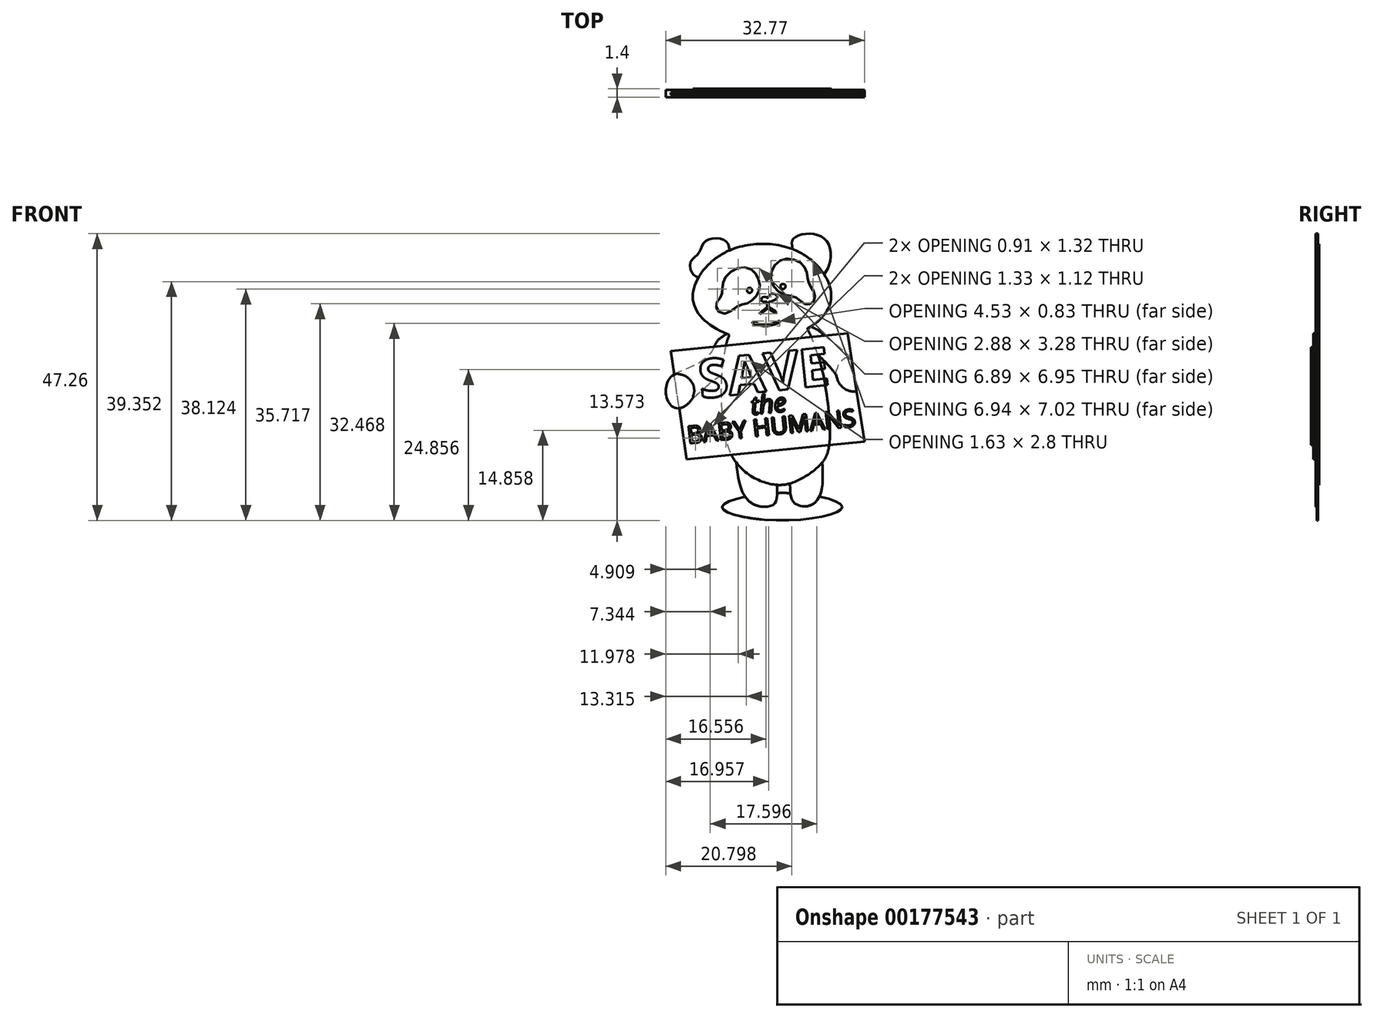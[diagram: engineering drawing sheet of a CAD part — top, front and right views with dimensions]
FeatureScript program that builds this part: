
annotation { "Feature Type Name" : "Feature", "Feature Type Description" : "" }
export const myFeature = defineFeature(function(context is Context, id is Id, definition is map)
    precondition{}
    {
        {
            var Q0;
            Q0=qCreatedBy(makeId("Front.planeOp"),FACE);
            var sketch = newSketch(context, id + "F0", { "sketchPlane" : qUnion([Q0])});
            skFitSpline(sketch, "E0", {"points": [v(-5.28, 20.68) * mm, v(-7.35, 19.05) * mm, v(-7.73, 17.53) * mm, v(-7.93, 16.12) * mm, v(-8.6, 15.23) * mm, v(-8.65, 13.83) * mm, v(-7.17, 13.2) * mm, v(-5.14, 14.5) * mm, v(-3.7, 14.88) * mm, v(-2.4, 15.83) * mm, v(-1.67, 17.32) * mm, v(-1.8, 18.83) * mm, v(-2.96, 20.4) * mm, v(-5.28, 20.68) * mm]});
            skCircle(sketch, "E1", {"center": v(-3.3, 17.01) * mm, "radius": 0.42 * mm});
            skPoint(sketch, "E1.first.point", {"position": v(-3.3, 17.43) * mm});
            skPoint(sketch, "E1.second.point", {"position": v(-3.71, 16.96) * mm});
            skPoint(sketch, "E1.third.point", {"position": v(-2.98, 16.74) * mm});
            skFitSpline(sketch, "E2", {"points": [v(1.76, 21.94) * mm, v(0.2, 19.14) * mm, v(2.09, 16.4) * mm, v(4.27, 15.86) * mm, v(5.92, 14.74) * mm, v(7.23, 15.16) * mm, v(7.35, 16.75) * mm, v(6.47, 18.12) * mm, v(6.17, 19.96) * mm, v(4.8, 21.76) * mm, v(1.76, 21.94) * mm]});
            skCircle(sketch, "E3", {"center": v(2.22, 17.66) * mm, "radius": 0.42 * mm});
            skPoint(sketch, "E3.first.point", {"position": v(2.1, 18.06) * mm});
            skPoint(sketch, "E3.second.point", {"position": v(2.6, 17.5) * mm});
            skPoint(sketch, "E3.third.point", {"position": v(1.93, 17.36) * mm});
            skArc(sketch, "E4", {"start": v(-2.65, 11.8) * mm, "mid": v(-0.55, 11.38) * mm, "end": v(1.52, 11.95) * mm});
            skArc(sketch, "E5.0", {"start": v(-2.76, 11.58) * mm, "mid": v(-0.54, 11.13) * mm, "end": v(1.64, 11.73) * mm});
            skArc(sketch, "E6", {"start": v(-2.65, 11.8) * mm, "mid": v(-2.82, 11.75) * mm, "end": v(-2.76, 11.58) * mm});
            skArc(sketch, "E7", {"start": v(1.64, 11.73) * mm, "mid": v(1.69, 11.9) * mm, "end": v(1.52, 11.95) * mm});
            skLineSegment(sketch, "E8", {"start": v(-0.37, 15.1) * mm, "end": v(-0.37, 14.25) * mm});
            skLineSegment(sketch, "E9", {"start": v(-0.37, 14.25) * mm, "end": v(-1.56, 13.38) * mm});
            skLineSegment(sketch, "E10", {"start": v(-1.4, 13.18) * mm, "end": v(-0.25, 14.04) * mm});
            skLineSegment(sketch, "E11", {"start": v(-0.25, 14.04) * mm, "end": v(0.84, 13.34) * mm});
            skLineSegment(sketch, "E12", {"start": v(0.97, 13.55) * mm, "end": v(-0.12, 14.25) * mm});
            skArc(sketch, "E13", {"start": v(-1.56, 13.38) * mm, "mid": v(-1.58, 13.2) * mm, "end": v(-1.4, 13.18) * mm});
            skArc(sketch, "E14", {"start": v(0.84, 13.34) * mm, "mid": v(1.01, 13.38) * mm, "end": v(0.97, 13.55) * mm});
            skLineSegment(sketch, "E15", {"start": v(-0.12, 14.25) * mm, "end": v(-0.12, 15.1) * mm});
            skLineSegment(sketch, "E16", {"start": v(-0.12, 14.25) * mm, "end": v(-0.37, 14.25) * mm, "construction": true});
            skLineSegment(sketch, "E17", {"start": v(-0.25, 14.04) * mm, "end": v(-0.25, 14.25) * mm, "construction": true});
            skFitSpline(sketch, "E18", {"points": [v(-0.12, 15.1) * mm, v(0.96, 15.47) * mm, v(1.28, 16) * mm, v(0.76, 16.41) * mm, v(0.1, 16.32) * mm, v(-0.34, 15.75) * mm, v(-0.55, 15.87) * mm, v(-1.21, 15.83) * mm, v(-1.3, 15.26) * mm, v(-0.37, 15.1) * mm], "startDerivative": vector(11.63, 3.5) * mm, "endDerivative": vector(9.76, -0.12) * mm});
            skFitSpline(sketch, "E19", {"points": [v(-2.63, 24.6) * mm, v(-9.81, 21.5) * mm, v(-12.55, 14.98) * mm, v(-4.94, 9.22) * mm, v(7.09, 11.26) * mm, v(10.15, 16.53) * mm, v(5.87, 22.76) * mm, v(-2.63, 24.6) * mm]});
            skFitSpline(sketch, "E20", {"points": [v(9.02, 19.63) * mm, v(10.01, 21.92) * mm, v(9.55, 24.92) * mm, v(7.54, 26.24) * mm, v(4.8, 26.07) * mm, v(3.75, 25.22) * mm, v(3.79, 23.8) * mm], "startDerivative": vector(7.2, 11.9) * mm, "endDerivative": vector(1.85, -11.75) * mm});
            skFitSpline(sketch, "E21", {"points": [v(-6.58, 23.6) * mm, v(-7.17, 25.08) * mm, v(-9.3, 25.6) * mm, v(-10.91, 24.76) * mm, v(-11.7, 23.08) * mm, v(-12.97, 21.79) * mm, v(-12.73, 19.83) * mm, v(-11.73, 19.13) * mm], "startDerivative": vector(-2.26, 12.84) * mm, "endDerivative": vector(9.74, -4.03) * mm});
            skLineSegment(sketch, "E22", {"start": v(-16.26, 7) * mm, "end": v(12.87, 9.94) * mm});
            skLineSegment(sketch, "E23", {"start": v(12.87, 9.94) * mm, "end": v(15.65, -7.93) * mm});
            skLineSegment(sketch, "E24", {"start": v(15.65, -7.93) * mm, "end": v(-13.67, -10.86) * mm});
            skLineSegment(sketch, "E25", {"start": v(-13.67, -10.86) * mm, "end": v(-16.26, 7) * mm});
            skFitSpline(sketch, "E26", {"points": [v(-6.63, 9.7) * mm, v(-7.92, -2.36) * mm, v(-5.2, -11.77) * mm, v(1.02, -15.04) * mm, v(4.98, -14.16) * mm, v(8.4, -11.7) * mm, v(9.84, -8.51) * mm, v(9.3, 0.7) * mm, v(6.24, 10.75) * mm], "startDerivative": vector(-22.93, -59.57) * mm, "endDerivative": vector(-34.57, 71.29) * mm});
            skFitSpline(sketch, "E27", {"points": [v(1.24, -15.06) * mm, v(1.05, -17.83) * mm, v(0.16, -18.54) * mm, v(-1.53, -18.61) * mm, v(-3.1, -17.97) * mm, v(-4.6, -15.86) * mm, v(-5.5, -11.37) * mm], "startDerivative": vector(0.14, -22.55) * mm, "endDerivative": vector(-2, 15.97) * mm});
            skFitSpline(sketch, "E28", {"points": [v(3.35, -14.83) * mm, v(3.85, -17.76) * mm, v(5.22, -18.57) * mm, v(7.4, -18.06) * mm, v(8.67, -15.36) * mm, v(8.68, -11.38) * mm], "startDerivative": vector(0.57, -23.36) * mm, "endDerivative": vector(-0.75, 13.96) * mm});
            skFitSpline(sketch, "E29", {"points": [v(-7.08, 9.86) * mm, v(-8.5, 8.78) * mm, v(-9.06, 7.87) * mm, v(-9.71, 6.7) * mm, v(-11.13, 5.35) * mm, v(-13.33, 4.22) * mm, v(-15.15, 3.31) * mm, v(-13.96, 2.94) * mm, v(-12.6, 1.46) * mm, v(-12.43, 0.2) * mm, v(-12.59, -0.63) * mm, v(-7.9, 3.1) * mm], "startDerivative": vector(-20.24, -14.92) * mm, "endDerivative": vector(48, 30.85) * mm});
            skFitSpline(sketch, "E30", {"points": [v(6.73, 11.03) * mm, v(8.93, 9.71) * mm, v(13.27, 6.03) * mm, v(12.9, 6) * mm, v(11.36, 4.7) * mm, v(11, 3.2) * mm, v(8.01, 6.33) * mm], "startDerivative": vector(19.92, -7.63) * mm, "endDerivative": vector(-37.46, 34.17) * mm});
            skFitSpline(sketch, "E31", {"points": [v(-15.15, 3.31) * mm, v(-16.84, 1.82) * mm, v(-17, -0.51) * mm, v(-15.8, -2.28) * mm, v(-14.43, -2.3) * mm, v(-12.59, -0.63) * mm], "startDerivative": vector(-13.86, -3.67) * mm, "endDerivative": vector(8.5, 13.26) * mm});
            skFitSpline(sketch, "E32", {"points": [v(13.27, 6.03) * mm, v(15.18, 4.93) * mm, v(15.77, 2.37) * mm, v(14.8, 0.57) * mm, v(13.17, 0.44) * mm, v(10.97, 3.13) * mm], "startDerivative": vector(17.85, -0.45) * mm, "endDerivative": vector(-4.75, 22.55) * mm});
            skFitSpline(sketch, "E33.trimOffspring", {"points": [v(-7.08, 9.86) * mm, v(-8.5, 8.78) * mm, v(-9.06, 7.87) * mm, v(-9.71, 6.7) * mm, v(-11.13, 5.35) * mm, v(-13.33, 4.22) * mm, v(-15.15, 3.31) * mm, v(-13.96, 2.94) * mm, v(-12.6, 1.46) * mm, v(-12.43, 0.2) * mm, v(-12.59, -0.63) * mm, v(-7.9, 3.1) * mm], "startDerivative": vector(-20.24, -14.92) * mm, "endDerivative": vector(48, 30.85) * mm});
            skFitSpline(sketch, "E34", {"points": [v(-15.15, 3.31) * mm, v(-13.96, 2.94) * mm, v(-12.87, 1.95) * mm, v(-12.43, 0.77) * mm, v(-12.59, -0.63) * mm], "startDerivative": vector(4.13, 0.65) * mm, "endDerivative": vector(-1.58, -1.83) * mm});
            skFitSpline(sketch, "E35", {"points": [v(10.97, 3.13) * mm, v(11.69, 4.98) * mm, v(13.27, 6.03) * mm], "startDerivative": vector(-0.55, 3.17) * mm, "endDerivative": vector(2.92, 0.17) * mm});
            skSolve(sketch);
        }
        {
            var Q0;
            Q0=makeQuery(id+"F0.imprint","IMPRINT",FACE,{"disambiguationData":[TD([[makeQuery(id+"F0.imprint","IMPRINT",EDGE,{"derivedFrom":sQuery(id+"F0.wireOp",EDGE,"E0")}),-1.0]])]});
            var Q1;
            Q1=makeQuery(id+"F0.imprint","IMPRINT",FACE,{"disambiguationData":[TD([[makeQuery(id+"F0.imprint","IMPRINT",EDGE,{"derivedFrom":sQuery(id+"F0.wireOp",EDGE,"E1")}),1.0]])]});
            var Q2;
            Q2=makeQuery(id+"F0.imprint","IMPRINT",FACE,{"disambiguationData":[TD([[makeQuery(id+"F0.imprint","IMPRINT",EDGE,{"derivedFrom":sQuery(id+"F0.wireOp",EDGE,"E3")}),1.0]])]});
            var Q3;
            {var subQ1=sQuery(id+"F0.wireOp",EDGE,"E26");var subQ7=sQuery(id+"F0.wireOp",EDGE,"E24");var subQ9=makeQuery(id+"F0.imprint","INTERSECT",VERTEX,{"disambiguationData":[OD(0.0)],"derivedFrom":[subQ7,subQ1]});Q3=makeQuery(id+"F0.imprint","IMPRINT",FACE,{"disambiguationData":[TD([[makeQuery(id+"F0.imprint","IMPRINT",EDGE,{"disambiguationData":[TD([[subQ9,-1.0]])],"derivedFrom":subQ7}),1.0]])]});}
            var Q4;
            {var subQ0=sQuery(id+"F0.wireOp",EDGE,"E26");var subQ1=sQuery(id+"F0.wireOp",EDGE,"E22");var subQ2=makeQuery(id+"F0.imprint","INTERSECT",VERTEX,{"disambiguationData":[OD(0.0)],"derivedFrom":[subQ1,subQ0]});Q4=makeQuery(id+"F0.imprint","IMPRINT",FACE,{"disambiguationData":[TD([[makeQuery(id+"F0.imprint","IMPRINT",EDGE,{"disambiguationData":[TD([[subQ2,-1.0]])],"derivedFrom":subQ1}),-1.0]])]});}
            var Q5;
            {var subQ0=sQuery(id+"F0.wireOp",EDGE,"E26");var subQ1=sQuery(id+"F0.wireOp",EDGE,"E19");var subQ2=makeQuery(id+"F0.imprint","INTERSECT",VERTEX,{"disambiguationData":[OD(0.0)],"derivedFrom":[subQ1,subQ0]});Q5=makeQuery(id+"F0.imprint","IMPRINT",FACE,{"disambiguationData":[TD([[makeQuery(id+"F0.imprint","IMPRINT",EDGE,{"disambiguationData":[TD([[subQ2,-1.0]])],"derivedFrom":subQ1}),-1.0]])]});}
            extrude(context, id + "F1", {"entities" : qUnion([Q0, Q1, Q2, Q3, Q4, Q5]), "depth" : .4 * mm});
        }
        {
            var Q0;
            Q0=makeQuery(id+"F0.imprint","IMPRINT",FACE,{"disambiguationData":[TD([[makeQuery(id+"F0.imprint","IMPRINT",EDGE,{"derivedFrom":sQuery(id+"F0.wireOp",EDGE,"E0")}),1.0]])]});
            var Q1;
            Q1=makeQuery(id+"F0.imprint","IMPRINT",FACE,{"disambiguationData":[TD([[makeQuery(id+"F0.imprint","IMPRINT",EDGE,{"derivedFrom":sQuery(id+"F0.wireOp",EDGE,"E2")}),1.0]])]});
            var Q2;
            {var subQ0=sQuery(id+"F0.wireOp",EDGE,"E20");Q2=makeQuery(id+"F0.imprint","IMPRINT",FACE,{"disambiguationData":[TD([[makeQuery(id+"F0.imprint","IMPRINT",EDGE,{"derivedFrom":subQ0}),1.0]])]});}
            var Q3;
            {var subQ0=sQuery(id+"F0.wireOp",EDGE,"E21");Q3=makeQuery(id+"F0.imprint","IMPRINT",FACE,{"disambiguationData":[TD([[makeQuery(id+"F0.imprint","IMPRINT",EDGE,{"derivedFrom":subQ0}),1.0]])]});}
            var Q4;
            Q4=makeQuery(id+"F0.imprint","IMPRINT",FACE,{"disambiguationData":[TD([[makeQuery(id+"F0.imprint","IMPRINT",EDGE,{"derivedFrom":sQuery(id+"F0.wireOp",EDGE,"E8")}),1.0]])]});
            var Q5;
            Q5=makeQuery(id+"F0.imprint","IMPRINT",FACE,{"disambiguationData":[TD([[makeQuery(id+"F0.imprint","IMPRINT",EDGE,{"derivedFrom":sQuery(id+"F0.wireOp",EDGE,"E4")}),-1.0]])]});
            var Q6;
            {var subQ0=sQuery(id+"F0.wireOp",EDGE,"E27");Q6=makeQuery(id+"F0.imprint","IMPRINT",FACE,{"disambiguationData":[TD([[makeQuery(id+"F0.imprint","IMPRINT",EDGE,{"derivedFrom":subQ0}),-1.0]])]});}
            var Q7;
            {var subQ0=sQuery(id+"F0.wireOp",EDGE,"E28");Q7=makeQuery(id+"F0.imprint","IMPRINT",FACE,{"disambiguationData":[TD([[makeQuery(id+"F0.imprint","IMPRINT",EDGE,{"derivedFrom":subQ0}),1.0]])]});}
            extrude(context, id + "F2", {"entities" : qUnion([Q0, Q1, Q2, Q3, Q4, Q5, Q6, Q7]), "depth" : .4 * mm});
        }
        {
            var Q0;
            {var subQ0=sQuery(id+"F0.wireOp",EDGE,"E29");var subQ1=sQuery(id+"F0.wireOp",EDGE,"E22");var subQ2=makeQuery(id+"F0.imprint","INTERSECT",VERTEX,{"derivedFrom":[subQ1,subQ0]});Q0=makeQuery(id+"F0.imprint","IMPRINT",FACE,{"disambiguationData":[TD([[makeQuery(id+"F0.imprint","IMPRINT",EDGE,{"disambiguationData":[TD([[subQ2,-1.0]])],"derivedFrom":subQ1}),-1.0]])]});}
            var Q1;
            {var subQ0=sQuery(id+"F0.wireOp",EDGE,"E26");var subQ1=sQuery(id+"F0.wireOp",EDGE,"E19");var subQ2=makeQuery(id+"F0.imprint","INTERSECT",VERTEX,{"disambiguationData":[OD(0.0)],"derivedFrom":[subQ1,subQ0]});Q1=makeQuery(id+"F0.imprint","IMPRINT",FACE,{"disambiguationData":[TD([[makeQuery(id+"F0.imprint","IMPRINT",EDGE,{"disambiguationData":[TD([[subQ2,1.0]])],"derivedFrom":subQ1}),-1.0]])]});}
            var Q2;
            {var subQ0=sQuery(id+"F0.wireOp",EDGE,"E26");var subQ1=sQuery(id+"F0.wireOp",EDGE,"E19");var subQ2=makeQuery(id+"F0.imprint","INTERSECT",VERTEX,{"disambiguationData":[OD(1.0)],"derivedFrom":[subQ1,subQ0]});Q2=makeQuery(id+"F0.imprint","IMPRINT",FACE,{"disambiguationData":[TD([[makeQuery(id+"F0.imprint","IMPRINT",EDGE,{"disambiguationData":[TD([[subQ2,-1.0]])],"derivedFrom":subQ1}),-1.0]])]});}
            var Q3;
            {var subQ0=sQuery(id+"F0.wireOp",EDGE,"E30");var subQ1=sQuery(id+"F0.wireOp",EDGE,"E22");var subQ2=makeQuery(id+"F0.imprint","INTERSECT",VERTEX,{"derivedFrom":[subQ1,subQ0]});Q3=makeQuery(id+"F0.imprint","IMPRINT",FACE,{"disambiguationData":[TD([[makeQuery(id+"F0.imprint","IMPRINT",EDGE,{"disambiguationData":[TD([[subQ2,1.0]])],"derivedFrom":subQ1}),-1.0]])]});}
            extrude(context, id + "F3", {"entities" : qUnion([Q0, Q1, Q2, Q3]), "depth" : .4 * mm});
        }
        {
            var Q0;
            Q0=makeQuery(id+"F1.opExtrude","CAP_FACE",FACE,{"disambiguationData":[OSD([sQuery(id+"F0.wireOp",EDGE,"E0"),sQuery(id+"F0.wireOp",EDGE,"E2"),sQuery(id+"F0.wireOp",EDGE,"E4"),sQuery(id+"F0.wireOp",EDGE,"E5.0"),sQuery(id+"F0.wireOp",EDGE,"E6"),sQuery(id+"F0.wireOp",EDGE,"E7"),sQuery(id+"F0.wireOp",EDGE,"E8"),sQuery(id+"F0.wireOp",EDGE,"E9"),sQuery(id+"F0.wireOp",EDGE,"E10"),sQuery(id+"F0.wireOp",EDGE,"E11"),sQuery(id+"F0.wireOp",EDGE,"E12"),sQuery(id+"F0.wireOp",EDGE,"E13"),sQuery(id+"F0.wireOp",EDGE,"E14"),sQuery(id+"F0.wireOp",EDGE,"E15"),sQuery(id+"F0.wireOp",EDGE,"E18"),sQuery(id+"F0.wireOp",EDGE,"E19"),sQuery(id+"F0.wireOp",EDGE,"E26")])],"isStart":false});
            var sketch = newSketch(context, id + "F4", { "sketchPlane" : qUnion([Q0])});
            skLineSegment(sketch, "E36.0", {"start": v(-13.67, -10.86) * mm, "end": v(-16.26, 7) * mm});
            skLineSegment(sketch, "E36.1", {"start": v(12.87, 9.94) * mm, "end": v(15.65, -7.93) * mm});
            skLineSegment(sketch, "E36.2", {"start": v(-16.26, 7) * mm, "end": v(12.87, 9.94) * mm});
            skLineSegment(sketch, "E36.3", {"start": v(15.65, -7.93) * mm, "end": v(-13.67, -10.86) * mm});
            skSolve(sketch);
        }
        {
            var Q0;
            Q0=qSketchRegion(id+"F4",true);
            extrude(context, id + "F5", {"entities" : qUnion([Q0]), "depth" : .4 * mm});
        }
        {
            var Q0;
            {var subQ0=sQuery(id+"F0.wireOp",EDGE,"E31");var subQ1=sQuery(id+"F0.wireOp",EDGE,"E25");var subQ2=makeQuery(id+"F0.imprint","INTERSECT",VERTEX,{"disambiguationData":[OD(0.0)],"derivedFrom":[subQ1,subQ0]});Q0=makeQuery(id+"F0.imprint","IMPRINT",FACE,{"disambiguationData":[TD([[makeQuery(id+"F0.imprint","IMPRINT",EDGE,{"disambiguationData":[TD([[subQ2,-1.0]])],"derivedFrom":subQ1}),-1.0]])]});}
            var Q1;
            {var subQ0=sQuery(id+"F0.wireOp",EDGE,"E31");var subQ1=sQuery(id+"F0.wireOp",EDGE,"E25");var subQ2=makeQuery(id+"F0.imprint","INTERSECT",VERTEX,{"disambiguationData":[OD(0.0)],"derivedFrom":[subQ1,subQ0]});Q1=makeQuery(id+"F0.imprint","IMPRINT",FACE,{"disambiguationData":[TD([[makeQuery(id+"F0.imprint","IMPRINT",EDGE,{"disambiguationData":[TD([[subQ2,-1.0]])],"derivedFrom":subQ1}),1.0]])]});}
            var Q2;
            {var subQ0=sQuery(id+"F0.wireOp",EDGE,"E32");var subQ1=sQuery(id+"F0.wireOp",EDGE,"E23");var subQ2=makeQuery(id+"F0.imprint","INTERSECT",VERTEX,{"disambiguationData":[OD(0.0)],"derivedFrom":[subQ1,subQ0]});Q2=makeQuery(id+"F0.imprint","IMPRINT",FACE,{"disambiguationData":[TD([[makeQuery(id+"F0.imprint","IMPRINT",EDGE,{"disambiguationData":[TD([[subQ2,-1.0]])],"derivedFrom":subQ1}),1.0]])]});}
            var Q3;
            {var subQ0=sQuery(id+"F0.wireOp",EDGE,"E32");var subQ1=sQuery(id+"F0.wireOp",EDGE,"E23");var subQ2=makeQuery(id+"F0.imprint","INTERSECT",VERTEX,{"disambiguationData":[OD(0.0)],"derivedFrom":[subQ1,subQ0]});Q3=makeQuery(id+"F0.imprint","IMPRINT",FACE,{"disambiguationData":[TD([[makeQuery(id+"F0.imprint","IMPRINT",EDGE,{"disambiguationData":[TD([[subQ2,-1.0]])],"derivedFrom":subQ1}),-1.0]])]});}
            extrude(context, id + "F6", {"entities" : qUnion([Q0, Q1, Q2, Q3]), "depth" : (.8 + .4) * mm});
        }
        {
            var Q0;
            Q0=makeQuery(id+"F5.opExtrude","CAP_FACE",FACE,{"disambiguationData":[OSD([sQuery(id+"F4.wireOp",EDGE,"E36.0"),sQuery(id+"F4.wireOp",EDGE,"E36.1"),sQuery(id+"F4.wireOp",EDGE,"E36.2"),sQuery(id+"F4.wireOp",EDGE,"E36.3")])],"isStart":false});
            var sketch = newSketch(context, id + "F7", { "sketchPlane" : qUnion([Q0])});
            skText(sketch, "E37", { "text": "SAVE", "fontName": "OpenSans-Bold.ttf"});
            skText(sketch, "E38", { "text": "the", "fontName": "OpenSans-Italic.ttf"});
            skText(sketch, "E39", { "text": "BABY HUMANS", "fontName": "OpenSans-Regular.ttf"});
            const initialGuessF7  = {"E37": [-0.0114, -0.0008, 0.99462, 0.10357, 0.00635], "E38": [-0.00296, -0.0035, 0.99462, 0.10357, 0.00303], "E39": [-0.01345, -0.00826, 0.99462, 0.10357, 0.00285]};
            skSetInitialGuess(sketch, initialGuessF7);
            skSolve(sketch);
        }
        {
            var Q0;
            Q0=qSketchRegion(id+"F7",true);
            extrude(context, id + "F8", {"entities" : qUnion([Q0]), "depth" : .4 * mm});
        }
        {
            var Q0;
            Q0=qCreatedBy(makeId("Front.planeOp"),FACE);
            var sketch = newSketch(context, id + "F9", { "sketchPlane" : qUnion([Q0])});
            skFitSpline(sketch, "E40", {"points": [v(2.23, -16.4) * mm, v(-7.8, -18.75) * mm, v(2.25, -20.92) * mm, v(11.98, -18.72) * mm, v(2.23, -16.4) * mm]});
            skSolve(sketch);
        }
        {
            var Q0;
            Q0=makeQuery(id+"F9.imprint","IMPRINT",FACE,{"disambiguationData":[TD([[makeQuery(id+"F9.imprint","IMPRINT",EDGE,{"derivedFrom":sQuery(id+"F9.wireOp",EDGE,"E40")}),1.0]])]});
            extrude(context, id + "F10", {"entities" : qUnion([Q0]), "depth" : .2 * mm});
        }
        {
            var Q0;
            Q0=makeQuery(id+"F2.opExtrude","SWEPT_BODY",BODY,{"disambiguationData":[OSD([sQuery(id+"F0.wireOp",EDGE,"E26"),sQuery(id+"F0.wireOp",EDGE,"E27")])]});
            var Q1;
            Q1=makeQuery(id+"F2.opExtrude","SWEPT_BODY",BODY,{"disambiguationData":[OSD([sQuery(id+"F0.wireOp",EDGE,"E26"),sQuery(id+"F0.wireOp",EDGE,"E28")])]});
            var Q2;
            Q2=makeQuery(id+"F10.opExtrude","SWEPT_BODY",BODY,{"disambiguationData":[OSD([sQuery(id+"F9.wireOp",EDGE,"E40")])]});
            booleanBodies(context, id + "F11", {"operationType" : BooleanOperationType.SUBTRACTION, "tools" : qUnion([Q0, Q1]), "targets" : qUnion([Q2]), "keepTools" : true});
        }
        {
            var Q0;
            Q0=makeQuery(id+"F0.imprint","IMPRINT",FACE,{"disambiguationData":[TD([[makeQuery(id+"F0.imprint","IMPRINT",EDGE,{"derivedFrom":sQuery(id+"F0.wireOp",EDGE,"E0")}),-1.0]])]});
            var Q1;
            Q1=makeQuery(id+"F0.imprint","IMPRINT",FACE,{"disambiguationData":[TD([[makeQuery(id+"F0.imprint","IMPRINT",EDGE,{"derivedFrom":sQuery(id+"F0.wireOp",EDGE,"E2")}),1.0]])]});
            var Q2;
            Q2=makeQuery(id+"F0.imprint","IMPRINT",FACE,{"disambiguationData":[TD([[makeQuery(id+"F0.imprint","IMPRINT",EDGE,{"derivedFrom":sQuery(id+"F0.wireOp",EDGE,"E0")}),1.0]])]});
            var Q3;
            Q3=makeQuery(id+"F0.imprint","IMPRINT",FACE,{"disambiguationData":[TD([[makeQuery(id+"F0.imprint","IMPRINT",EDGE,{"derivedFrom":sQuery(id+"F0.wireOp",EDGE,"E1")}),1.0]])]});
            var Q4;
            Q4=makeQuery(id+"F0.imprint","IMPRINT",FACE,{"disambiguationData":[TD([[makeQuery(id+"F0.imprint","IMPRINT",EDGE,{"derivedFrom":sQuery(id+"F0.wireOp",EDGE,"E3")}),1.0]])]});
            var Q5;
            Q5=makeQuery(id+"F0.imprint","IMPRINT",FACE,{"disambiguationData":[TD([[makeQuery(id+"F0.imprint","IMPRINT",EDGE,{"derivedFrom":sQuery(id+"F0.wireOp",EDGE,"E8")}),1.0]])]});
            var Q6;
            Q6=makeQuery(id+"F0.imprint","IMPRINT",FACE,{"disambiguationData":[TD([[makeQuery(id+"F0.imprint","IMPRINT",EDGE,{"derivedFrom":sQuery(id+"F0.wireOp",EDGE,"E4")}),-1.0]])]});
            var Q7;
            {var subQ0=sQuery(id+"F0.wireOp",EDGE,"E26");var subQ1=sQuery(id+"F0.wireOp",EDGE,"E19");var subQ2=makeQuery(id+"F0.imprint","INTERSECT",VERTEX,{"disambiguationData":[OD(0.0)],"derivedFrom":[subQ1,subQ0]});Q7=makeQuery(id+"F0.imprint","IMPRINT",FACE,{"disambiguationData":[TD([[makeQuery(id+"F0.imprint","IMPRINT",EDGE,{"disambiguationData":[TD([[subQ2,-1.0]])],"derivedFrom":subQ1}),-1.0]])]});}
            var Q8;
            {var subQ0=sQuery(id+"F0.wireOp",EDGE,"E26");var subQ5=sQuery(id+"F0.wireOp",EDGE,"E22");var subQ6=makeQuery(id+"F0.imprint","INTERSECT",VERTEX,{"disambiguationData":[OD(0.0)],"derivedFrom":[subQ5,subQ0]});Q8=makeQuery(id+"F0.imprint","IMPRINT",FACE,{"disambiguationData":[TD([[makeQuery(id+"F0.imprint","IMPRINT",EDGE,{"disambiguationData":[TD([[subQ6,-1.0]])],"derivedFrom":subQ5}),-1.0]])]});}
            var Q9;
            {var subQ1=sQuery(id+"F0.wireOp",EDGE,"E26");var subQ6=sQuery(id+"F0.wireOp",EDGE,"E24");var subQ9=makeQuery(id+"F0.imprint","INTERSECT",VERTEX,{"disambiguationData":[OD(0.0)],"derivedFrom":[subQ6,subQ1]});Q9=makeQuery(id+"F0.imprint","IMPRINT",FACE,{"disambiguationData":[TD([[makeQuery(id+"F0.imprint","IMPRINT",EDGE,{"disambiguationData":[TD([[subQ9,-1.0]])],"derivedFrom":subQ6}),1.0]])]});}
            extrude(context, id + "F12", {"entities" : qUnion([Q0, Q1, Q2, Q3, Q4, Q5, Q6, Q7, Q8, Q9]), "oppositeDirection" : true, "depth" : .2 * mm});
        }
    });
